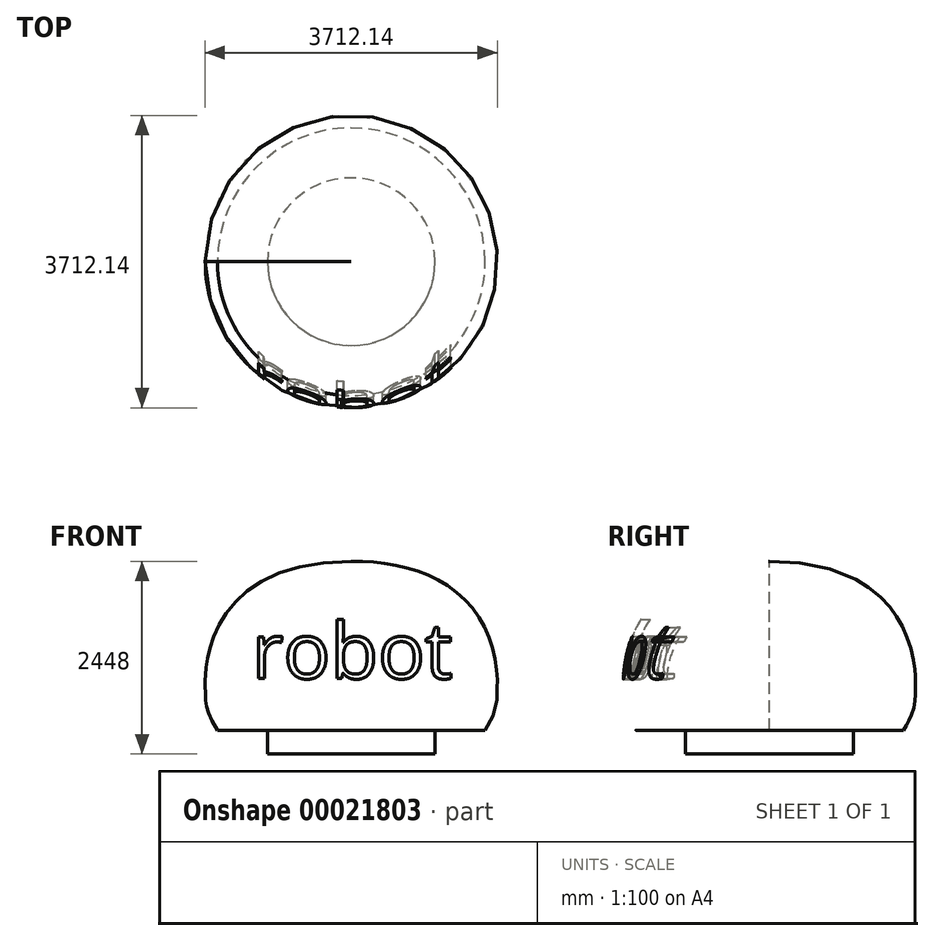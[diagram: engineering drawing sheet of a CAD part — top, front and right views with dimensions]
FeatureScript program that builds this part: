
annotation { "Feature Type Name" : "Feature", "Feature Type Description" : "" }
export const myFeature = defineFeature(function(context is Context, id is Id, definition is map)
    precondition{}
    {
        {
            var Q0;
            Q0=qCreatedBy(makeId("Front.planeOp"),FACE);
            var sketch = newSketch(context, id + "F0", { "sketchPlane" : qUnion([Q0])});
            skFitSpline(sketch, "E0", {"points": [v(-1700, 0) * mm, v(-1853, 500) * mm, v(-1853, 701.93) * mm, v(0, 2148) * mm], "startDerivative": vector(-1918.05, 2940.86) * mm, "endDerivative": vector(8710.13, 0) * mm});
            skLineSegment(sketch, "E1", {"start": v(-1853, 1762.23) * mm, "end": v(-1853, -185.32) * mm, "construction": true});
            skLineSegment(sketch, "E2", {"start": v(0, 2660.4) * mm, "end": v(0, -1878.13) * mm});
            skLineSegment(sketch, "E3", {"start": v(-1700, 0) * mm, "end": v(0, 0) * mm});
            skLineSegment(sketch, "E4", {"start": v(0, 0) * mm, "end": v(0, 2148) * mm});
            skSolve(sketch);
        }
        {
            var Q0;
            {var subQ2=sQuery(id+"F0.wireOp",EDGE,"E0");Q0=makeQuery(id+"F0.imprint","IMPRINT",FACE,{"disambiguationData":[TD([[makeQuery(id+"F0.imprint","IMPRINT",EDGE,{"derivedFrom":subQ2}),-1.0]])]});}
            var Q1;
            Q1=sQuery(id+"F0.wireOp",EDGE,"E0");
            var Q2;
            Q2=sQuery(id+"F0.wireOp",EDGE,"E2");
            revolve(context, id + "F1", {"entities" : qUnion([Q0]), "surfaceEntities" : qUnion([Q1]), "axis" : qUnion([Q2]), "revolveType" : RevolveType.FULL});
        }
        {
            var Q0;
            Q0=qCreatedBy(makeId("Front.planeOp"),FACE);
            var sketch = newSketch(context, id + "F2", { "sketchPlane" : qUnion([Q0])});
            skLineSegment(sketch, "E5.bottom", {"start": v(0, 0) * mm, "end": v(-1065, 0) * mm});
            skLineSegment(sketch, "E5.top", {"start": v(0, -300) * mm, "end": v(-1065, -300) * mm});
            skLineSegment(sketch, "E5.left", {"start": v(0, 0) * mm, "end": v(0, -300) * mm});
            skLineSegment(sketch, "E5.right", {"start": v(-1065, 0) * mm, "end": v(-1065, -300) * mm});
            skSolve(sketch);
        }
        {
            var Q0;
            Q0=makeQuery(id+"F2.imprint","IMPRINT",FACE,{"disambiguationData":[TD([[makeQuery(id+"F2.imprint","IMPRINT",EDGE,{"derivedFrom":sQuery(id+"F2.wireOp",EDGE,"E5.bottom")}),1.0]])]});
            var Q1;
            Q1=sQuery(id+"F0.wireOp",EDGE,"E2");
            revolve(context, id + "F3", {"operationType" : NewBodyOperationType.ADD, "entities" : qUnion([Q0]), "axis" : qUnion([Q1]), "revolveType" : RevolveType.FULL});
        }
        {
            var Q0;
            Q0=qCreatedBy(makeId("Front.planeOp"),FACE);
            var sketch = newSketch(context, id + "F4", { "sketchPlane" : qUnion([Q0])});
            skFitSpline(sketch, "E6.0", {"points": [v(-1616.24, 54.63) * mm, v(-1634.95, 83.31) * mm, v(-1667.17, 137.1) * mm, v(-1696.27, 195.83) * mm, v(-1713.99, 238.11) * mm, v(-1724.78, 267.58) * mm, v(-1733.36, 294.94) * mm, v(-1740.01, 320.36) * mm, v(-1745.01, 344.02) * mm, v(-1748.62, 366.11) * mm, v(-1751.07, 386.87) * mm, v(-1752.58, 406.53) * mm, v(-1753.36, 425.35) * mm, v(-1753.55, 440.56) * mm, v(-1753.53, 452.6) * mm, v(-1753.44, 461.58) * mm, v(-1753.31, 470.57) * mm, v(-1753.2, 478.1) * mm, v(-1753.11, 484.18) * mm, v(-1753.06, 488.76) * mm, v(-1753.02, 493.37) * mm, v(-1753, 496.86) * mm, v(-1753, 499.2) * mm, v(-1753, 500.77) * mm, v(-1753, 503.5) * mm, v(-1753.03, 507.33) * mm, v(-1753.08, 511.86) * mm, v(-1753.15, 516.3) * mm, v(-1753.24, 520.68) * mm, v(-1753.38, 526.41) * mm, v(-1753.59, 533.41) * mm, v(-1753.88, 541.57) * mm, v(-1754.3, 552.2) * mm, v(-1754.86, 565.09) * mm, v(-1755.45, 580.42) * mm, v(-1755.9, 596.18) * mm, v(-1756.11, 613) * mm, v(-1756.04, 628.37) * mm, v(-1755.77, 641.77) * mm, v(-1755.45, 652.45) * mm, v(-1755, 663.8) * mm, v(-1754.4, 675.9) * mm, v(-1753.66, 688.78) * mm, v(-1752.74, 702.54) * mm, v(-1751.64, 717.08) * mm, v(-1750.33, 732.37) * mm, v(-1748.8, 748.4) * mm, v(-1746.45, 770.69) * mm, v(-1742.86, 800.24) * mm, v(-1737.36, 838.17) * mm, v(-1730.5, 878.34) * mm, v(-1719.38, 934.59) * mm, v(-1701.36, 1009.34) * mm, v(-1671.98, 1104.33) * mm, v(-1633.68, 1202.78) * mm, v(-1585.3, 1302.94) * mm, v(-1525.71, 1403.1) * mm, v(-1453.7, 1501.66) * mm, v(-1367.97, 1597.05) * mm, v(-1267.15, 1687.77) * mm, v(-1149.7, 1772.29) * mm, v(-1014, 1849) * mm, v(-858.39, 1916.18) * mm, v(-681.18, 1971.97) * mm, v(-480.79, 2014.43) * mm, v(-255.72, 2041.53) * mm, v(-88.29, 2048) * mm, v(0, 2048) * mm]});
            skSolve(sketch);
        }
        {
            var Q0;
            Q0 = qSketchRegion(id + "F4", true);
            var Q1;
            Q1=sQuery(id+"F4.wireOp",EDGE,"E6.0");
            var Q2;
            Q2=sQuery(id+"F0.wireOp",EDGE,"E2");
            revolve(context, id + "F5", {"bodyType" : ToolBodyType.SURFACE, "entities" : qUnion([Q0]), "surfaceEntities" : qUnion([Q1]), "axis" : qUnion([Q2]), "revolveType" : RevolveType.FULL});
        }
        {
            var Q0;
            Q0=qCreatedBy(makeId("Front.planeOp"),FACE);
            var sketch = newSketch(context, id + "F6", { "sketchPlane" : qUnion([Q0])});
            skFitSpline(sketch, "E7.0", {"points": [v(-1700, 0) * mm, v(-1870.87, 262) * mm, v(-1841.9, 494.68) * mm, v(-1883.45, 734.3) * mm, v(-1645.2, 2148) * mm, v(0, 2148) * mm]});
            skSolve(sketch);
        }
        {
            var Q0;
            Q0 = qSketchRegion(id + "F6", true);
            var Q1;
            Q1=sQuery(id+"F6.wireOp",EDGE,"E7.0");
            var Q2;
            Q2=sQuery(id+"F0.wireOp",EDGE,"E2");
            revolve(context, id + "F7", {"bodyType" : ToolBodyType.SURFACE, "entities" : qUnion([Q0]), "surfaceEntities" : qUnion([Q1]), "axis" : qUnion([Q2]), "revolveType" : RevolveType.FULL});
        }
        {
            var Q0;
            Q0=qCreatedBy(makeId("Front.planeOp"),FACE);
            var sketch = newSketch(context, id + "F8", { "sketchPlane" : qUnion([Q0])});
            skText(sketch, "E8", { "text": "robot\n", "fontName": "OpenSans-Regular.ttf"});
            const initialGuessF8  = {"E8": [-1.26506, 0.65723, 1, 0, 0.71125]};
            skSetInitialGuess(sketch, initialGuessF8);
            skSolve(sketch);
        }
        {
            var Q0;
            Q0 = qSketchRegion(id + "F8", true);
            var Q1;
            Q1=makeQuery(id+"F7.opRevolve","SWEPT_FACE",FACE,{"disambiguationData":[OSD([sQuery(id+"F6.wireOp",EDGE,"E7.0")])]});
            extrude(context, id + "F9", {"entities" : qUnion([Q0]), "operationType" : NewBodyOperationType.REMOVE, "endBound" : BoundingType.UP_TO_SURFACE, "endBoundEntityFace" : qUnion([Q1]), "depth" : 25 * mm, "hasSecondDirection" : true, "secondDirectionBound" : SecondDirectionBoundingType.UP_TO_NEXT, "secondDirectionOppositeDirection" : false, "secondDirectionDepth" : 25 * mm});
        }
    });
